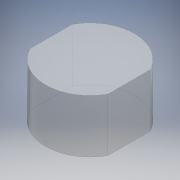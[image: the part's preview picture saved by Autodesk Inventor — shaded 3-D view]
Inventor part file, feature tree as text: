
AUTODESK INVENTOR PART (.ipt)
format: ipt  version: 2016 (Build 200138000, 138)  size: 99,328 bytes
history: native  units: mm
features: extrude x2, sketch x1
ambient origin geometry x8: Origin, YZ Plane, XZ Plane, XY Plane, X Axis, Y Axis, Z Axis, Center Point
bodies: Solid1 (feature_tree)
feature tree (3):
  sketch  "Sketch1"  dims[d0=2.5mm d1=1.5mm d2=0.0mm d3=2.2mm d4=0.2mm d5=0.0mm]
  extrude  "Extrusion1"  Depth=1.5mm TaperAngle=0.0deg
  extrude  "Extrusion2"  Depth=2.2mm
